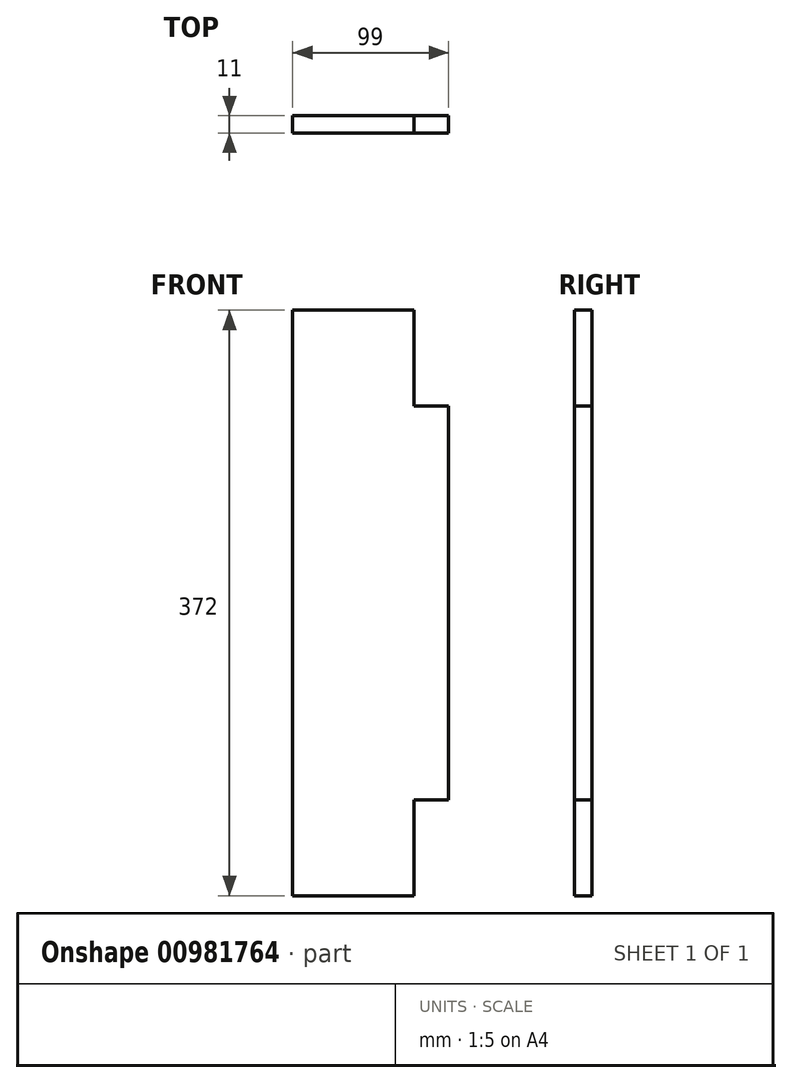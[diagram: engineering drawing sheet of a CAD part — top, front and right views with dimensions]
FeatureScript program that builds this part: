
annotation { "Feature Type Name" : "Feature", "Feature Type Description" : "" }
export const myFeature = defineFeature(function(context is Context, id is Id, definition is map)
    precondition{}
    {
        {
            var Q0;
            Q0=qCreatedBy(makeId("Front.planeOp"),FACE);
            var sketch = newSketch(context, id + "F0", { "sketchPlane" : qUnion([Q0])});
            skLineSegment(sketch, "E0", {"start": v(-49.5, 186) * mm, "end": v(27.5, 186) * mm});
            skLineSegment(sketch, "E1", {"start": v(-49.5, -186) * mm, "end": v(27.5, -186) * mm});
            skLineSegment(sketch, "E2", {"start": v(-49.5, 186) * mm, "end": v(-49.5, -186) * mm});
            skLineSegment(sketch, "E3", {"start": v(27.5, 186) * mm, "end": v(27.5, 125) * mm});
            skLineSegment(sketch, "E4", {"start": v(27.5, -125) * mm, "end": v(27.5, -186) * mm});
            skLineSegment(sketch, "E5", {"start": v(49.5, -125) * mm, "end": v(49.5, 125) * mm});
            skLineSegment(sketch, "E6", {"start": v(27.5, -125) * mm, "end": v(49.5, -125) * mm});
            skLineSegment(sketch, "E7", {"start": v(27.5, 125) * mm, "end": v(49.5, 125) * mm});
            skSolve(sketch);
        }
        {
            var Q0;
            Q0=makeQuery(id+"F0.imprint","IMPRINT",FACE,{"disambiguationData":[TD([[makeQuery(id+"F0.imprint","IMPRINT",EDGE,{"derivedFrom":sQuery(id+"F0.wireOp",EDGE,"E0")}),-1.0]])]});
            extrude(context, id + "F1", {"entities" : qUnion([Q0]), "depth" : 11 * mm, "offsetDistance" : 25 * mm});
        }
    });
